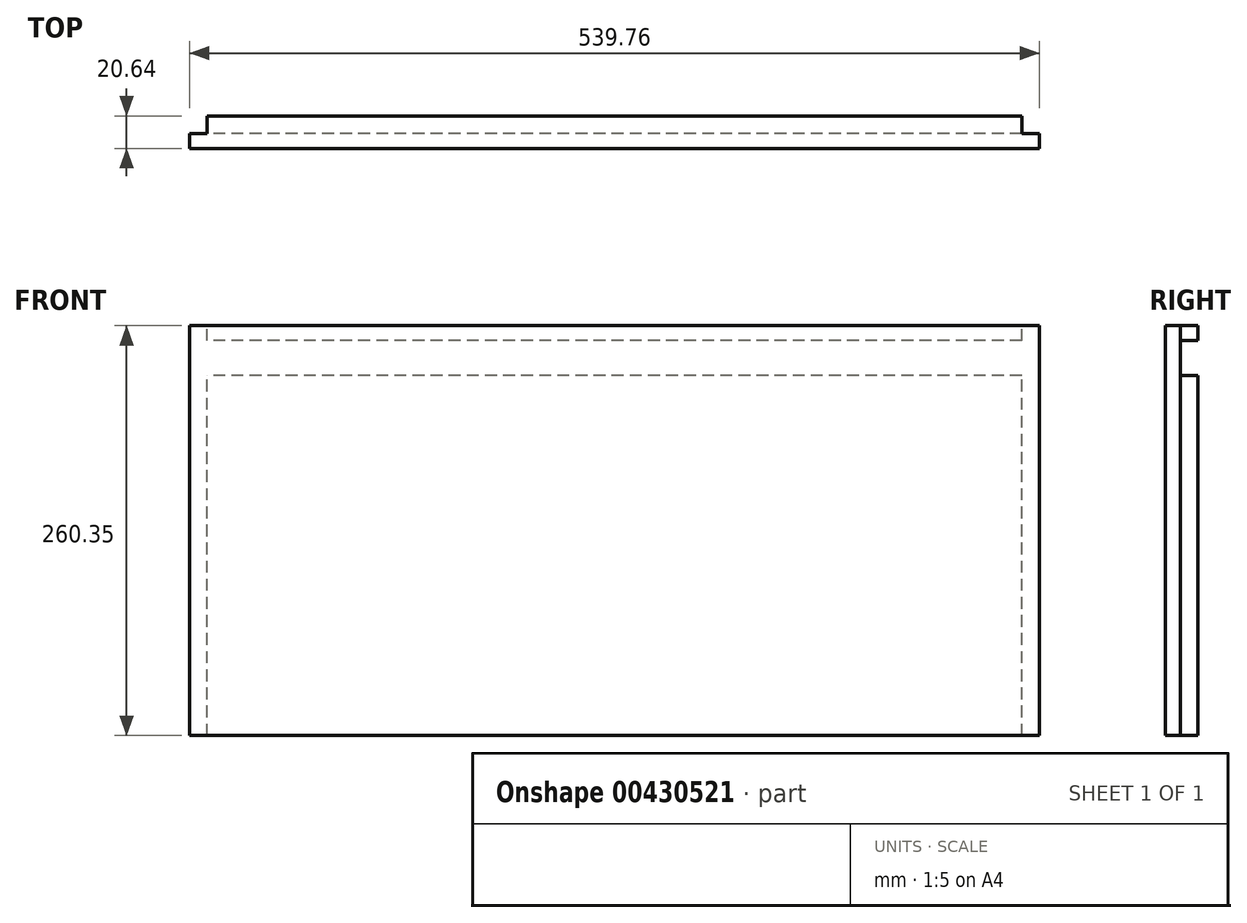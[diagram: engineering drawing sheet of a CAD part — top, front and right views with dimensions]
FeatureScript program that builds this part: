
annotation { "Feature Type Name" : "Feature", "Feature Type Description" : "" }
export const myFeature = defineFeature(function(context is Context, id is Id, definition is map)
    precondition{}
    {
        {
            var Q0;
            Q0=qCreatedBy(makeId("Top.planeOp"),FACE);
            var sketch = newSketch(context, id + "F0", { "sketchPlane" : qUnion([Q0])});
            skLineSegment(sketch, "E0", {"start": v(-269.88, 0) * mm, "end": v(269.88, 0) * mm});
            skLineSegment(sketch, "E1", {"start": v(269.88, 0) * mm, "end": v(269.88, 20.64) * mm});
            skLineSegment(sketch, "E2", {"start": v(269.88, 20.64) * mm, "end": v(-269.88, 20.64) * mm});
            skLineSegment(sketch, "E3", {"start": v(-269.88, 20.64) * mm, "end": v(-269.88, 0) * mm});
            skSolve(sketch);
        }
        {
            var Q0;
            Q0=makeQuery(id+"F0.imprint","IMPRINT",FACE,{"disambiguationData":[TD([[makeQuery(id+"F0.imprint","IMPRINT",EDGE,{"derivedFrom":sQuery(id+"F0.wireOp",EDGE,"E0")}),1.0]])]});
            extrude(context, id + "F1", {"entities" : qUnion([Q0]), "oppositeDirection" : true, "depth" : 260.35 * mm});
        }
        {
            var Q0;
            Q0=makeQuery(id+"F1.opExtrude","CAP_FACE",FACE,{"disambiguationData":[OSD([sQuery(id+"F0.wireOp",EDGE,"E0"),sQuery(id+"F0.wireOp",EDGE,"E1"),sQuery(id+"F0.wireOp",EDGE,"E2"),sQuery(id+"F0.wireOp",EDGE,"E3")])],"isStart":true});
            var sketch = newSketch(context, id + "F2", { "sketchPlane" : qUnion([Q0])});
            skLineSegment(sketch, "E4.bottom", {"start": v(-269.88, 20.64) * mm, "end": v(-258.76, 20.64) * mm});
            skLineSegment(sketch, "E4.top", {"start": v(-269.88, 9.53) * mm, "end": v(-258.76, 9.53) * mm});
            skLineSegment(sketch, "E4.left", {"start": v(-269.88, 20.64) * mm, "end": v(-269.88, 9.53) * mm});
            skLineSegment(sketch, "E4.right", {"start": v(-258.76, 20.64) * mm, "end": v(-258.76, 9.53) * mm});
            skLineSegment(sketch, "E5.bottom", {"start": v(269.88, 20.64) * mm, "end": v(258.76, 20.64) * mm});
            skLineSegment(sketch, "E5.top", {"start": v(269.88, 9.53) * mm, "end": v(258.76, 9.53) * mm});
            skLineSegment(sketch, "E5.left", {"start": v(269.88, 20.64) * mm, "end": v(269.88, 9.53) * mm});
            skLineSegment(sketch, "E5.right", {"start": v(258.76, 20.64) * mm, "end": v(258.76, 9.53) * mm});
            skSolve(sketch);
        }
        {
            var Q0;
            Q0 = qSketchRegion(id + "F2", true);
            extrude(context, id + "F3", {"entities" : qUnion([Q0]), "operationType" : NewBodyOperationType.REMOVE, "endBound" : BoundingType.THROUGH_ALL, "oppositeDirection" : true, "depth" : 25.4 * mm});
        }
        {
            var Q0;
            Q0=makeQuery(id+"F1.opExtrude","SWEPT_FACE",FACE,{"disambiguationData":[OSD([sQuery(id+"F0.wireOp",EDGE,"E2")])]});
            var sketch = newSketch(context, id + "F4", { "sketchPlane" : qUnion([Q0])});
            skLineSegment(sketch, "E6.bottom", {"start": v(-258.76, -31.75) * mm, "end": v(258.76, -31.75) * mm});
            skLineSegment(sketch, "E6.top", {"start": v(-258.76, -9.53) * mm, "end": v(258.76, -9.53) * mm});
            skLineSegment(sketch, "E6.left", {"start": v(-258.76, -31.75) * mm, "end": v(-258.76, -9.53) * mm});
            skLineSegment(sketch, "E6.right", {"start": v(258.76, -31.75) * mm, "end": v(258.76, -9.53) * mm});
            skSolve(sketch);
        }
        {
            var Q0;
            Q0=makeQuery(id+"F4.imprint","IMPRINT",FACE,{"disambiguationData":[TD([[makeQuery(id+"F4.imprint","IMPRINT",EDGE,{"derivedFrom":sQuery(id+"F4.wireOp",EDGE,"E6.bottom")}),1.0]])]});
            var Q1;
            Q1=makeQuery(id+"F3.boolean.opBoolean","COPY",FACE,{"derivedFrom":makeQuery(id+"F3.opExtrude","SWEPT_FACE",FACE,{"disambiguationData":[OSD([sQuery(id+"F2.wireOp",EDGE,"E4.top")])]})});
            extrude(context, id + "F5", {"entities" : qUnion([Q0]), "operationType" : NewBodyOperationType.REMOVE, "endBound" : BoundingType.UP_TO_SURFACE, "oppositeDirection" : true, "endBoundEntityFace" : qUnion([Q1]), "depth" : 3 / 203.2 * mm, "offsetDistance" : 25.4 * mm});
        }
    });
